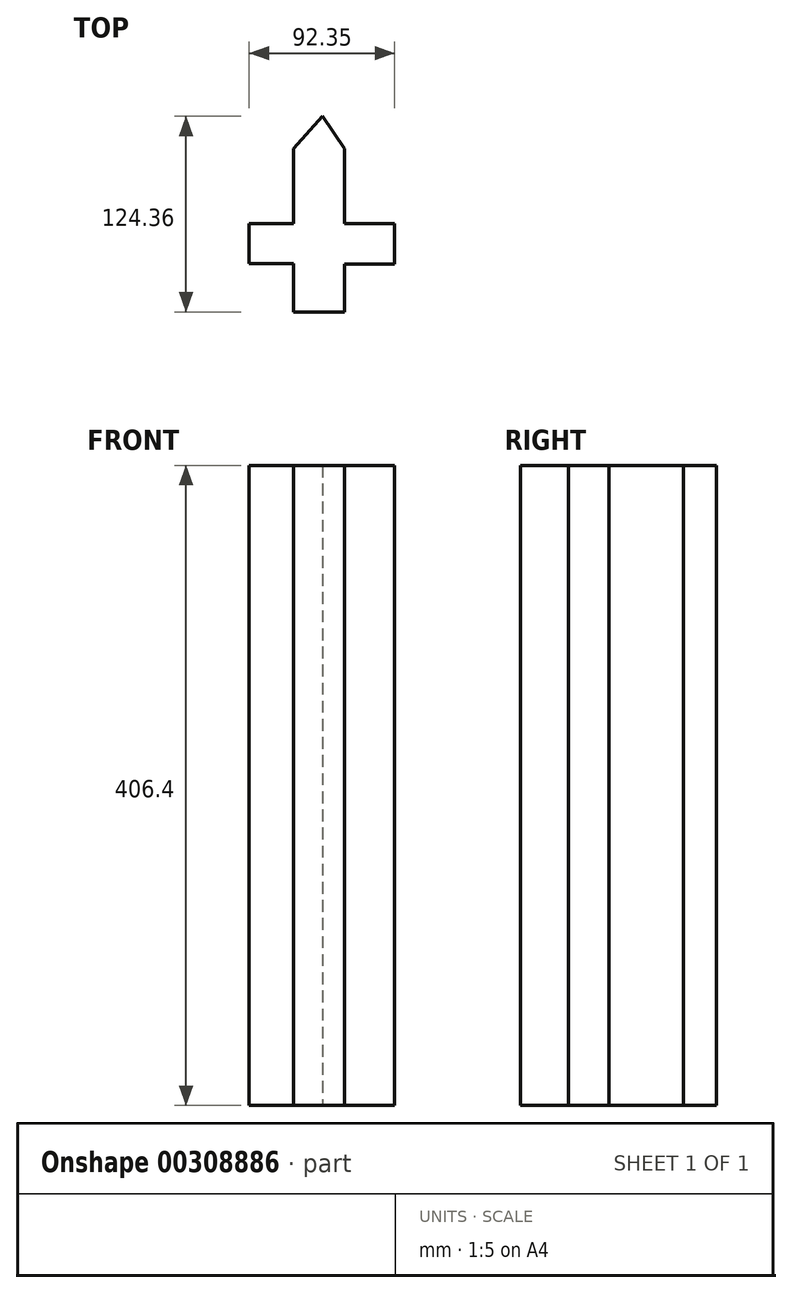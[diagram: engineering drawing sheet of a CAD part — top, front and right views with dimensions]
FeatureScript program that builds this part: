
annotation { "Feature Type Name" : "Feature", "Feature Type Description" : "" }
export const myFeature = defineFeature(function(context is Context, id is Id, definition is map)
    precondition{}
    {
        {
            var Q0;
            Q0=qCreatedBy(makeId("Top.planeOp"),FACE);
            var sketch = newSketch(context, id + "F0", { "sketchPlane" : qUnion([Q0])});
            skLineSegment(sketch, "E0", {"start": v(-18.29, -18.75) * mm, "end": v(-18.29, -49.53) * mm});
            skLineSegment(sketch, "E1", {"start": v(-18.29, -49.53) * mm, "end": v(14.02, -49.53) * mm});
            skLineSegment(sketch, "E2", {"start": v(14.02, -49.53) * mm, "end": v(14.02, -19.05) * mm});
            skLineSegment(sketch, "E3", {"start": v(-18.29, -18.75) * mm, "end": v(-46.63, -18.75) * mm});
            skLineSegment(sketch, "E4", {"start": v(14.02, -19.05) * mm, "end": v(45.72, -19.05) * mm});
            skLineSegment(sketch, "E5", {"start": v(-46.63, -18.75) * mm, "end": v(-46.63, 6.55) * mm});
            skLineSegment(sketch, "E6", {"start": v(-46.63, 6.55) * mm, "end": v(-18.29, 6.55) * mm});
            skLineSegment(sketch, "E7", {"start": v(-18.29, 6.55) * mm, "end": v(-18.29, 54.1) * mm});
            skLineSegment(sketch, "E8", {"start": v(-18.29, 54.1) * mm, "end": v(0, 74.83) * mm});
            skLineSegment(sketch, "E9", {"start": v(0, 74.83) * mm, "end": v(14.02, 54.1) * mm});
            skLineSegment(sketch, "E10", {"start": v(14.02, 54.1) * mm, "end": v(14.02, 6.55) * mm});
            skLineSegment(sketch, "E11", {"start": v(14.02, 6.55) * mm, "end": v(45.72, 6.55) * mm});
            skLineSegment(sketch, "E12", {"start": v(45.72, 6.55) * mm, "end": v(45.72, -19.05) * mm});
            skSolve(sketch);
        }
        {
            var Q0;
            Q0=makeQuery(id+"F0.imprint","IMPRINT",FACE,{"disambiguationData":[TD([[makeQuery(id+"F0.imprint","IMPRINT",EDGE,{"derivedFrom":sQuery(id+"F0.wireOp",EDGE,"E0")}),1.0]])]});
            extrude(context, id + "F1", {"entities" : qUnion([Q0]), "depth" : 406.4 * mm});
        }
    });
